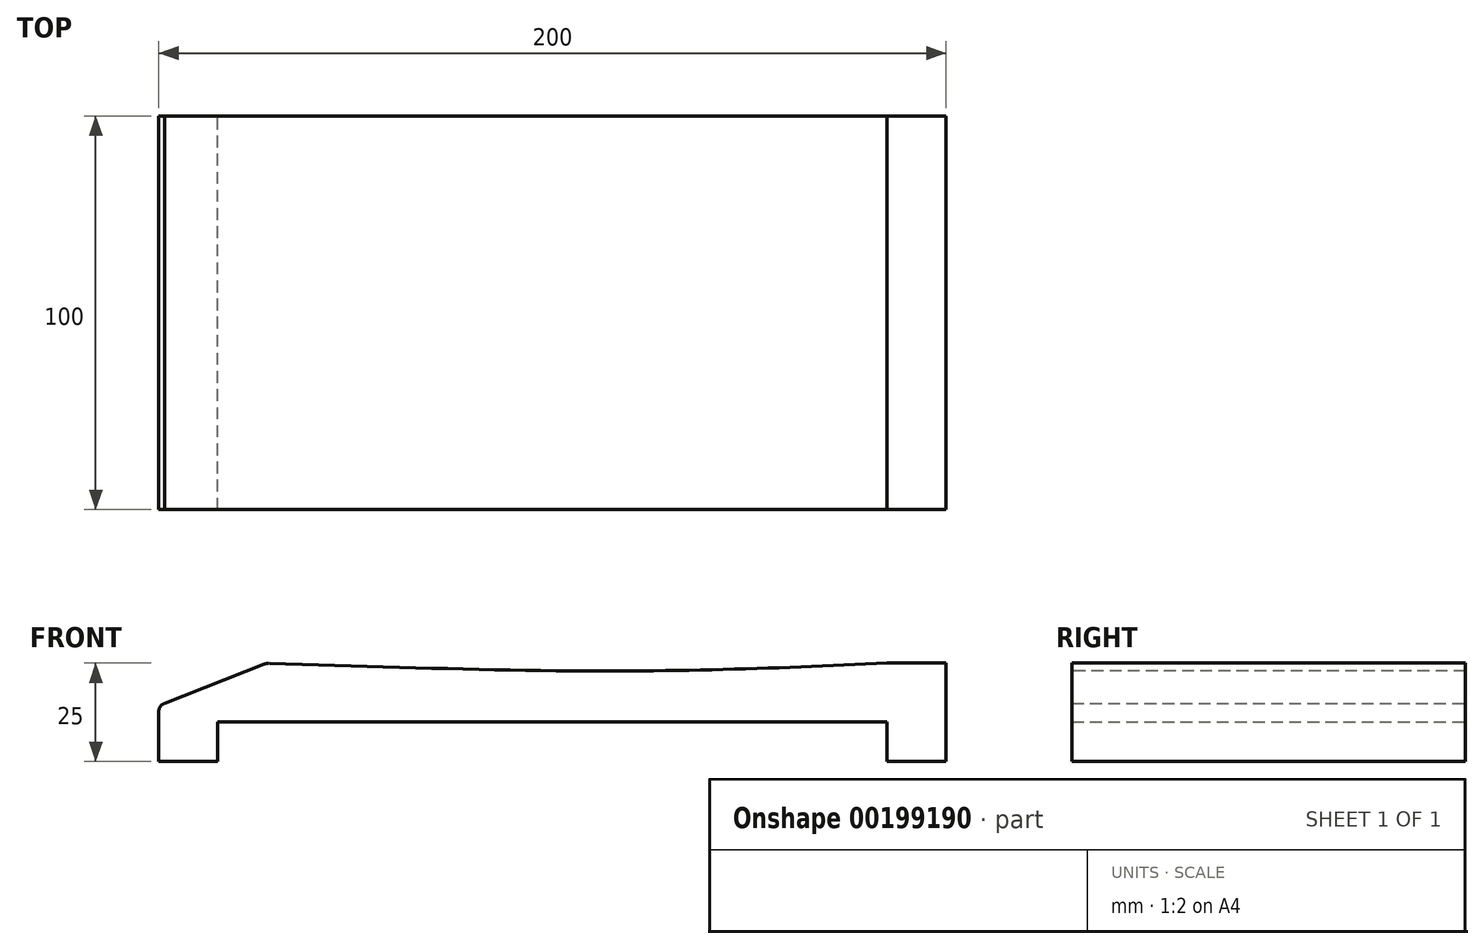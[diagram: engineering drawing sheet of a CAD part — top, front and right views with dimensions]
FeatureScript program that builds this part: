
annotation { "Feature Type Name" : "Feature", "Feature Type Description" : "" }
export const myFeature = defineFeature(function(context is Context, id is Id, definition is map)
    precondition{}
    {
        {
            var Q0;
            Q0=qCreatedBy(makeId("Front.planeOp"),FACE);
            var sketch = newSketch(context, id + "F0", { "sketchPlane" : qUnion([Q0])});
            skLineSegment(sketch, "E0", {"start": v(135.07, 0) * mm, "end": v(135.07, 25) * mm});
            skLineSegment(sketch, "E1", {"start": v(-64.93, 12.8) * mm, "end": v(-64.93, 0) * mm});
            skLineSegment(sketch, "E2", {"start": v(-64.93, 0) * mm, "end": v(-49.93, 0) * mm});
            skLineSegment(sketch, "E3", {"start": v(-49.93, 0) * mm, "end": v(-49.93, 10.1) * mm});
            skLineSegment(sketch, "E4", {"start": v(-49.93, 10.1) * mm, "end": v(120.07, 10.1) * mm});
            skLineSegment(sketch, "E5", {"start": v(120.07, 10.1) * mm, "end": v(120.07, 0) * mm});
            skLineSegment(sketch, "E6", {"start": v(120.07, 0) * mm, "end": v(135.07, 0) * mm});
            skPoint(sketch, "E7.visualSharp", {"position": v(-64.93, 14.33) * mm});
            skArc(sketch, "E7.filletArc", {"start": v(-63.46, 14.73) * mm, "mid": v(-64.52, 14.02) * mm, "end": v(-64.93, 12.8) * mm});
            skLineSegment(sketch, "E8", {"start": v(54.65, 25) * mm, "end": v(54.65, 23) * mm});
            skPoint(sketch, "E8.endSnap0", {"position": v(54.65, 25) * mm});
            skLineSegment(sketch, "E9", {"start": v(-63.46, 14.73) * mm, "end": v(-38.01, 24.77) * mm});
            skLineSegment(sketch, "E10", {"start": v(135.07, 25) * mm, "end": v(120.07, 25) * mm});
            skFitSpline(sketch, "E11", {"points": [v(-37.43, 25) * mm, v(54.65, 23) * mm, v(120.07, 25) * mm], "startDerivative": vector(176.95, -5.87) * mm, "endDerivative": vector(136.92, 6.22) * mm});
            skArc(sketch, "E12.filletArc", {"start": v(-36.8, 24.98) * mm, "mid": v(-37.42, 24.94) * mm, "end": v(-38.01, 24.77) * mm});
            skSolve(sketch);
        }
        {
            var Q0;
            Q0 = qSketchRegion(id + "F0", true);
            extrude(context, id + "F1", {"entities" : qUnion([Q0]), "depth" : 100 * mm});
        }
    });
